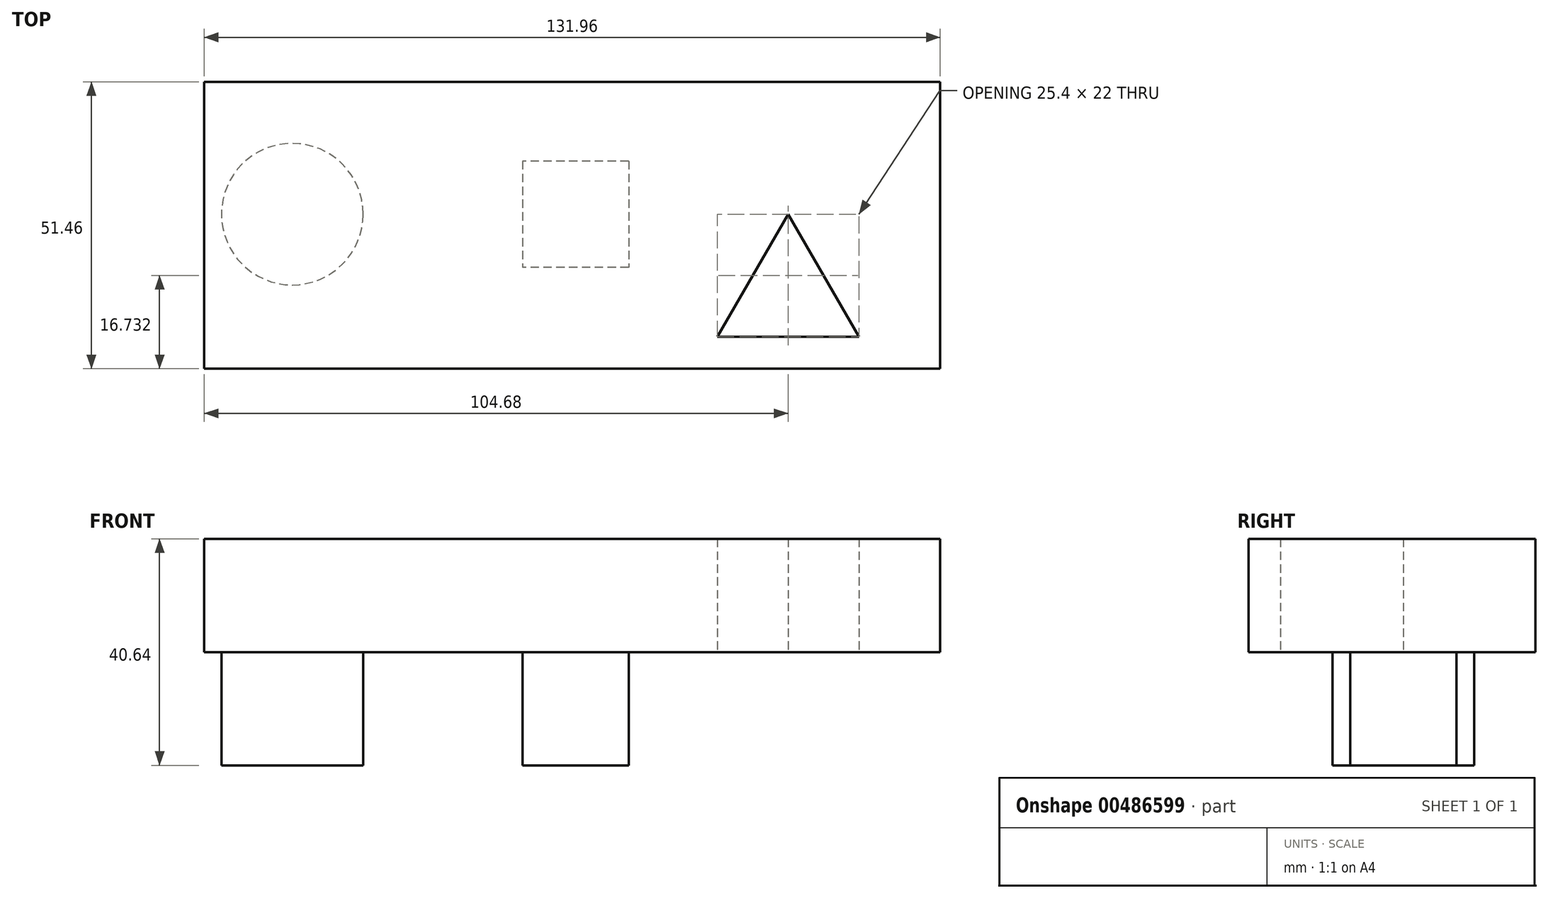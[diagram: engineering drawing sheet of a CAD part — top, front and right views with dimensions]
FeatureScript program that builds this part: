
annotation { "Feature Type Name" : "Feature", "Feature Type Description" : "" }
export const myFeature = defineFeature(function(context is Context, id is Id, definition is map)
    precondition{}
    {
        {
            var Q0;
            Q0=qCreatedBy(makeId("Top.planeOp"),FACE);
            var sketch = newSketch(context, id + "F0", { "sketchPlane" : qUnion([Q0])});
            skLineSegment(sketch, "E0", {"start": v(0, -26.3) * mm, "end": v(-31.75, -26.3) * mm});
            skLineSegment(sketch, "E1", {"start": v(-31.75, -26.3) * mm, "end": v(-82.55, -26.3) * mm});
            skLineSegment(sketch, "E2", {"start": v(-82.55, -26.3) * mm, "end": v(-82.55, 0) * mm});
            skLineSegment(sketch, "E3", {"start": v(-31.75, -26.3) * mm, "end": v(-31.75, 0) * mm});
            skLineSegment(sketch, "E4", {"start": v(0, 10.75) * mm, "end": v(6.35, 10.75) * mm});
            skLineSegment(sketch, "E5", {"start": v(6.35, 10.75) * mm, "end": v(6.35, 0) * mm});
            skLineSegment(sketch, "E6", {"start": v(6.35, 0) * mm, "end": v(19.05, -22) * mm});
            skLineSegment(sketch, "E7", {"start": v(19.05, -22) * mm, "end": v(-6.35, -22) * mm});
            skLineSegment(sketch, "E8", {"start": v(-6.35, -22) * mm, "end": v(6.35, 0) * mm});
            skLineSegment(sketch, "E9.bottom", {"start": v(-22.22, 9.53) * mm, "end": v(-41.27, 9.53) * mm});
            skLineSegment(sketch, "E9.top", {"start": v(-22.23, -9.53) * mm, "end": v(-41.27, -9.52) * mm});
            skLineSegment(sketch, "E9.left", {"start": v(-22.22, 9.53) * mm, "end": v(-22.22, -9.53) * mm});
            skLineSegment(sketch, "E9.right", {"start": v(-41.27, 9.53) * mm, "end": v(-41.27, -9.52) * mm});
            skPoint(sketch, "E9.middle", {"position": v(-31.75, 0) * mm});
            skCircle(sketch, "E10", {"center": v(-82.55, 0) * mm, "radius": 12.7 * mm});
            skSolve(sketch);
        }
        {
            var Q0;
            Q0=qCreatedBy(makeId("Top.planeOp"),FACE);
            var sketch = newSketch(context, id + "F1", { "sketchPlane" : qUnion([Q0])});
            skLineSegment(sketch, "E11.bottom", {"start": v(-98.33, -27.73) * mm, "end": v(33.63, -27.73) * mm});
            skLineSegment(sketch, "E11.top", {"start": v(-98.33, 23.73) * mm, "end": v(33.63, 23.73) * mm});
            skLineSegment(sketch, "E11.left", {"start": v(-98.33, -27.73) * mm, "end": v(-98.33, 23.73) * mm});
            skLineSegment(sketch, "E11.right", {"start": v(33.63, -27.73) * mm, "end": v(33.63, 23.73) * mm});
            skSolve(sketch);
        }
        {
            var Q0;
            Q0 = qSketchRegion(id + "F1", true);
            extrude(context, id + "F2", {"entities" : qUnion([Q0]), "depth" : 20.32 * mm});
        }
        {
            var Q0;
            Q0=makeQuery(id+"F0.imprint","IMPRINT",FACE,{"disambiguationData":[TD([[makeQuery(id+"F0.imprint","IMPRINT",EDGE,{"derivedFrom":sQuery(id+"F0.wireOp",EDGE,"E10")}),1.0]])]});
            var Q1;
            Q1=makeQuery(id+"F0.imprint","IMPRINT",FACE,{"disambiguationData":[TD([[makeQuery(id+"F0.imprint","IMPRINT",EDGE,{"derivedFrom":sQuery(id+"F0.wireOp",EDGE,"E9.bottom")}),1.0]])]});
            extrude(context, id + "F3", {"entities" : qUnion([Q0, Q1]), "operationType" : NewBodyOperationType.ADD, "oppositeDirection" : true, "depth" : 20.32 * mm});
        }
        {
            var Q0;
            Q0=makeQuery(id+"F0.imprint","IMPRINT",FACE,{"disambiguationData":[TD([[makeQuery(id+"F0.imprint","IMPRINT",EDGE,{"derivedFrom":sQuery(id+"F0.wireOp",EDGE,"E6")}),-1.0]])]});
            extrude(context, id + "F4", {"entities" : qUnion([Q0]), "operationType" : NewBodyOperationType.REMOVE, "depth" : 57.15 * mm});
        }
    });
